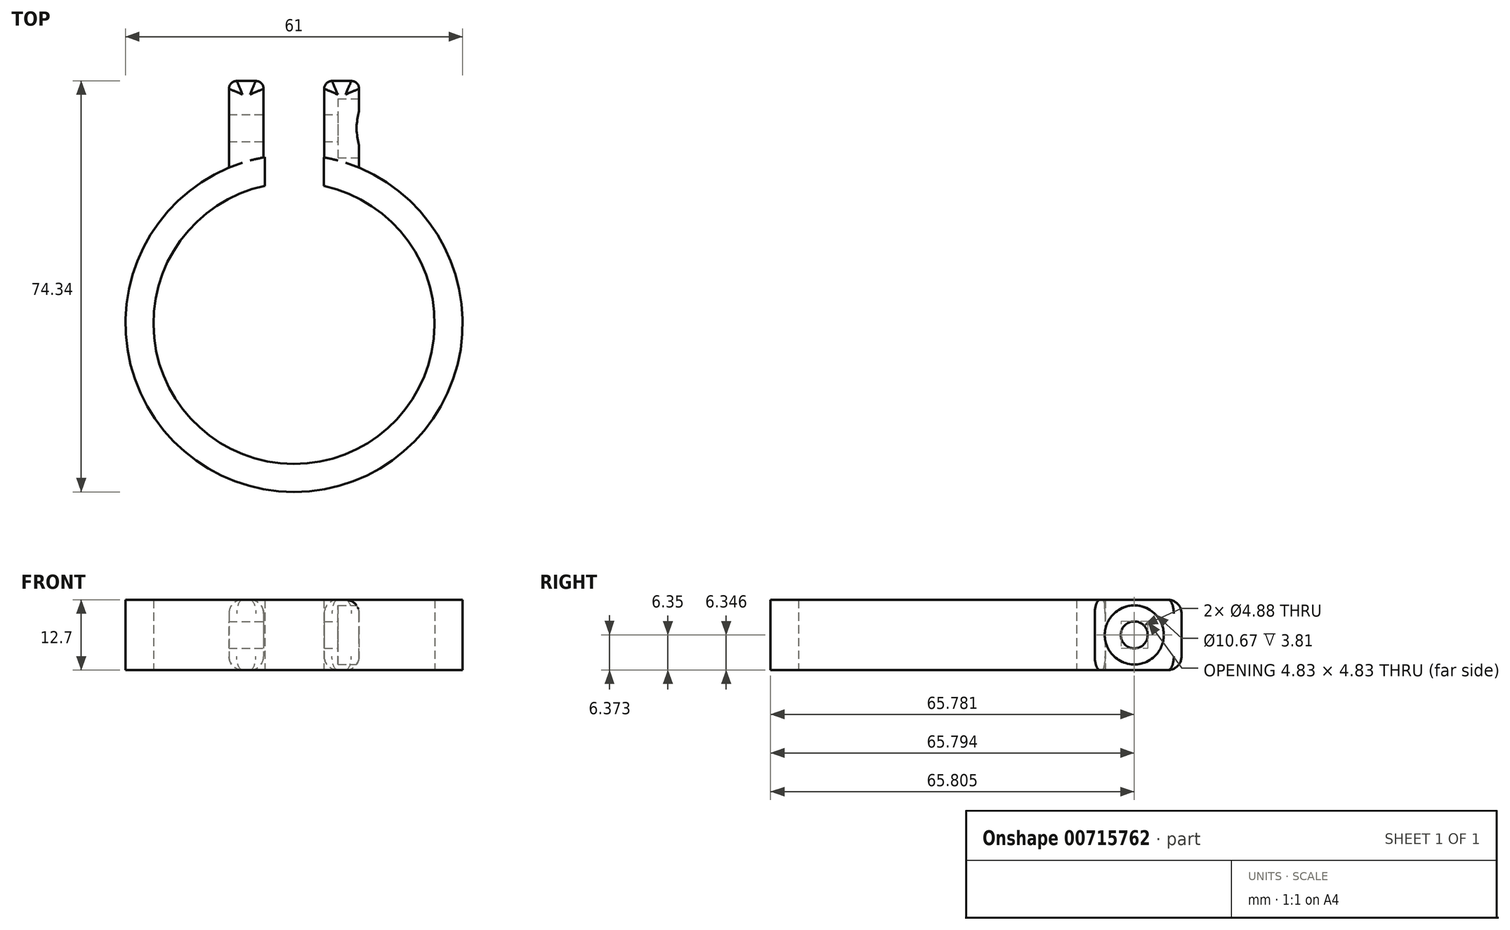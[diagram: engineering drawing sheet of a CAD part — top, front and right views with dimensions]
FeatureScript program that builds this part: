
annotation { "Feature Type Name" : "Feature", "Feature Type Description" : "" }
export const myFeature = defineFeature(function(context is Context, id is Id, definition is map)
    precondition{}
    {
        {
            var Q0;
            Q0=qCreatedBy(makeId("Top.planeOp"),FACE);
            var sketch = newSketch(context, id + "F0", { "sketchPlane" : qUnion([Q0])});
            skCircle(sketch, "E0", {"center": v(0, 0) * mm, "radius": 25.43 * mm});
            skCircle(sketch, "E1", {"center": v(0, 0) * mm, "radius": 30.5 * mm});
            skLineSegment(sketch, "E2", {"start": v(-5.5, 24.82) * mm, "end": v(-5.5, 43.84) * mm});
            skLineSegment(sketch, "E3", {"start": v(5.46, 24.83) * mm, "end": v(5.46, 43.84) * mm});
            skLineSegment(sketch, "E4", {"start": v(5.46, 43.84) * mm, "end": v(11.77, 43.84) * mm});
            skLineSegment(sketch, "E5", {"start": v(11.77, 43.84) * mm, "end": v(11.77, 22.54) * mm});
            skLineSegment(sketch, "E6", {"start": v(-5.5, 43.84) * mm, "end": v(-11.77, 43.84) * mm});
            skLineSegment(sketch, "E7", {"start": v(-11.77, 43.84) * mm, "end": v(-11.77, 22.54) * mm});
            skSolve(sketch);
        }
        {
            var Q0;
            Q0=qSketchRegion(id+"F0",true);
            extrude(context, id + "F1", {"entities" : qUnion([Q0]), "depth" : 12.7 * mm, "offsetDistance" : 25.4 * mm});
        }
        {
            var Q0;
            Q0=makeQuery(id+"F1.opExtrude","SWEPT_EDGE",EDGE,{"disambiguationData":[OSD([sQuery(id+"F0.wireOp",EDGE,"E2"),sQuery(id+"F0.wireOp",EDGE,"E6")])]});
            var Q1;
            Q1=makeQuery(id+"F1.opExtrude","SWEPT_EDGE",EDGE,{"disambiguationData":[OSD([sQuery(id+"F0.wireOp",EDGE,"E6"),sQuery(id+"F0.wireOp",EDGE,"E7")])]});
            var Q2;
            Q2=makeQuery(id+"F1.opExtrude","SWEPT_EDGE",EDGE,{"disambiguationData":[OSD([sQuery(id+"F0.wireOp",EDGE,"E3"),sQuery(id+"F0.wireOp",EDGE,"E4")])]});
            var Q3;
            Q3=makeQuery(id+"F1.opExtrude","SWEPT_EDGE",EDGE,{"disambiguationData":[OSD([sQuery(id+"F0.wireOp",EDGE,"E4"),sQuery(id+"F0.wireOp",EDGE,"E5")])]});
            fillet(context, id + "F2", {"entities" : qUnion([Q0, Q1, Q2, Q3]), "radius" : 1.41 * mm, "tangentPropagation" : true, "allowEdgeOverflow" : false});
        }
        {
            var Q0;
            Q0=makeQuery(id+"F1.opExtrude","CAP_EDGE",EDGE,{"disambiguationData":[OSD([sQuery(id+"F0.wireOp",EDGE,"E6")])],"isStart":false});
            var Q1;
            Q1=makeQuery(id+"F1.opExtrude","CAP_EDGE",EDGE,{"disambiguationData":[OSD([sQuery(id+"F0.wireOp",EDGE,"E6")])],"isStart":true});
            var Q2;
            Q2=makeQuery(id+"F1.opExtrude","CAP_EDGE",EDGE,{"disambiguationData":[OSD([sQuery(id+"F0.wireOp",EDGE,"E4")])],"isStart":false});
            var Q3;
            Q3=makeQuery(id+"F1.opExtrude","CAP_EDGE",EDGE,{"disambiguationData":[OSD([sQuery(id+"F0.wireOp",EDGE,"E4")])],"isStart":true});
            fillet(context, id + "F3", {"entities" : qUnion([Q0, Q1, Q2, Q3]), "radius" : 2.45 * mm, "tangentPropagation" : true, "allowEdgeOverflow" : false});
        }
        {
            var Q0;
            Q0=qCreatedBy(makeId("Top.planeOp"),FACE);
            var sketch = newSketch(context, id + "F4", { "sketchPlane" : qUnion([Q0])});
            skLineSegment(sketch, "E8.bottom", {"start": v(-5.27, 30.29) * mm, "end": v(5.4, 30.29) * mm});
            skLineSegment(sketch, "E8.top", {"start": v(-5.27, 18.47) * mm, "end": v(5.4, 18.47) * mm});
            skLineSegment(sketch, "E8.left", {"start": v(-5.27, 30.29) * mm, "end": v(-5.27, 18.47) * mm});
            skLineSegment(sketch, "E8.right", {"start": v(5.4, 30.29) * mm, "end": v(5.4, 18.47) * mm});
            skLineSegment(sketch, "E9.bottom", {"start": v(5.4, 30.29) * mm, "end": v(5.4, 30.29) * mm});
            skLineSegment(sketch, "E9.top", {"start": v(5.4, 33.5) * mm, "end": v(5.4, 33.5) * mm});
            skLineSegment(sketch, "E9.left", {"start": v(5.4, 30.29) * mm, "end": v(5.4, 33.5) * mm});
            skLineSegment(sketch, "E9.right", {"start": v(5.4, 30.29) * mm, "end": v(5.4, 33.5) * mm});
            skLineSegment(sketch, "E10.bottom", {"start": v(-5.27, 30.29) * mm, "end": v(-5.27, 30.29) * mm});
            skLineSegment(sketch, "E10.top", {"start": v(-5.27, 33.5) * mm, "end": v(-5.27, 33.5) * mm});
            skLineSegment(sketch, "E10.left", {"start": v(-5.27, 30.29) * mm, "end": v(-5.27, 33.5) * mm});
            skLineSegment(sketch, "E10.right", {"start": v(-5.27, 30.29) * mm, "end": v(-5.27, 33.5) * mm});
            skLineSegment(sketch, "E11.bottom", {"start": v(5.4, 33.5) * mm, "end": v(-5.27, 33.5) * mm});
            skLineSegment(sketch, "E11.top", {"start": v(5.4, 34.52) * mm, "end": v(-5.27, 34.52) * mm});
            skLineSegment(sketch, "E11.left", {"start": v(5.4, 33.5) * mm, "end": v(5.4, 34.52) * mm});
            skLineSegment(sketch, "E11.right", {"start": v(-5.27, 33.5) * mm, "end": v(-5.27, 34.52) * mm});
            skSolve(sketch);
        }
        {
            var Q0;
            Q0=qSketchRegion(id+"F4",true);
            extrude(context, id + "F5", {"entities" : qUnion([Q0]), "operationType" : NewBodyOperationType.REMOVE, "depth" : 43.43 * mm, "offsetDistance" : 25.4 * mm});
        }
        {
            var Q0;
            Q0=makeQuery(id+"F1.opExtrude","SWEPT_FACE",FACE,{"disambiguationData":[OSD([sQuery(id+"F0.wireOp",EDGE,"E5")])]});
            var sketch = newSketch(context, id + "F6", { "sketchPlane" : qUnion([Q0])});
            skCircle(sketch, "E12", {"center": v(35.28, 6.35) * mm, "radius": 2.44 * mm});
            skPoint(sketch, "E12.centerSnap0", {"position": v(42.43, 6.35) * mm});
            skPoint(sketch, "E12.centerSnap1", {"position": v(35.28, 10.25) * mm});
            skSolve(sketch);
        }
        {
            var Q0;
            Q0=qSketchRegion(id+"F6",true);
            extrude(context, id + "F7", {"entities" : qUnion([Q0]), "operationType" : NewBodyOperationType.REMOVE, "oppositeDirection" : true, "depth" : 25.4 * mm, "offsetDistance" : 25.4 * mm});
        }
        {
            var Q0;
            Q0=makeQuery(id+"F6.imprint","IMPRINT",FACE,{"disambiguationData":[TD([[makeQuery(id+"F6.imprint","IMPRINT",EDGE,{"derivedFrom":sQuery(id+"F6.wireOp",EDGE,"E12")}),-1.0]])]});
            var sketch = newSketch(context, id + "F8", { "sketchPlane" : qUnion([Q0])});
            skCircle(sketch, "E13", {"center": v(35.3, 6.35) * mm, "radius": 5.33 * mm});
            skSolve(sketch);
        }
        {
            var Q0;
            Q0=qSketchRegion(id+"F8",true);
            extrude(context, id + "F9", {"entities" : qUnion([Q0]), "operationType" : NewBodyOperationType.REMOVE, "oppositeDirection" : true, "depth" : 3.8 * mm, "offsetDistance" : 25.4 * mm});
        }
    });
